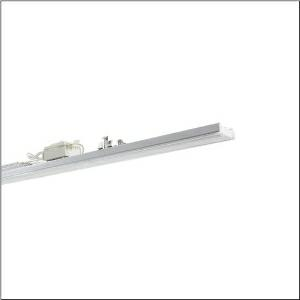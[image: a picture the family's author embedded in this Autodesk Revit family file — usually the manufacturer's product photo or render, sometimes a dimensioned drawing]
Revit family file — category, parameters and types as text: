
# Revit family: licross_21_recessed_mo_52tl11dn47xg
name_source: partatom
category: Lighting Fixtures
units: mm (PartAtom-declared; Revit-internal decimal feet)

## family parameters
Cut with Voids When Loaded = No
Host = Face
Light Source = No
Part Type = Normal
Room Calculation Point = No
Round Connector Dimension = Use Diameter
Shared = No

## types (1)
- --- (1 x LED, 7120 lm, 39.3 W, 4000K)
    Apparent Load = 39 VA
    CIE Flux Codes = 89 96 99 100 100
    Color Rendering = 80
    Color Temperature = 4000K
    Default Elevation = 1800 mm
    Description = Licross 21 Recessed MO, luminaire insert, of sheet steel, galvanised, coil coated, white, length: 1.500mm, width: 66mm, height: 67mm, LED rated luminous flux: 7.120lm, light colour: 840, SDCM (Standard Deviation of Colour Matching)MacAdam ≤ 3 SDCM (initial), control gear: DALI 2, with plug, 5-pole, with phase selection, mains connection: 220..240V, AC, 50/60Hz, rated input power: 39W, internal wiring halogen-free, primary light control with lens, of plastic, primary optical cover: cover, of PMMA, light emission: direct distribution, primary light characteristic: symmetric, protection rating (complete): IP40, insulation class (complete): insulation class I (protective earthing), certification: CE, ENEC, VDE, UKCA, protection symbol: D if used in an environment without relevant dust loads with corresponding accessories, impact resistance: IK06, permissible ambient temperature for indoor applications: -25..+40°C, corresponds to IFS (International Featured Standards) requirements for safety and quality in the food industry, reducing of maximum allowable ambient temperature of 5°C with ceiling mounting, LABS conformity tested according to VDMA 24364:2018-05, The light source and the operating device comply with the requirements of the Ecodesign Regulation (EU) 2019/2020 and are replaceable in accordance with this regulation, packaging unit: 1 piece
    Height = 58 mm
    Lamp = 1 x LED
    Lamp Light Flux = 7120 lm
    Lamp Power = 39.3 W
    Lamp count = 1
    Length = 1500 mm
    Luminous efficacy = 181 lm/W
    Manufacturer = Siteco
    ModVariant = No
    Model = 52TL11DN47XG
    Mounting Place = Ceiling
    Mounting Type = Pendant
    Number of Poles = 1
    OnlyDefault = Yes
    Power Factor = 1
    Product Name = Licross 21 Recessed MO
    Product group = luminaire insert | ceiling pendant
    ProductGroupID = 901
    Protection Class = Protection class I
    Protection Degree = IP 40
    RLX_Detail_Level = 1
    RLX_Emergency_Light_Flux = 0 lm
    RLX_Emergency_Type = 0
    RLX_Emergency_Type_DB = No
    RlxData = <blob elided: 24373 chars, md5=0a7918dd>
    Socket = socket
    Standby Power = 0 W
    System Light Flux = 7120 lm
    System Power = 39 W
    Type Comments = factory setting: luminous flux: 100 % | dim-lin: 254 | 267 mA
    Type Image = l_1296930.jpg
    URL = http://relux.com
    VarID = @adj_127095
    Voltage = 0 V
    Weight = 0.00 kg
    Width = 66 mm

## geometry (parser evidence)
native form markers: Blend x4, Sweep x12
no freeform markers — native parametric forms only
